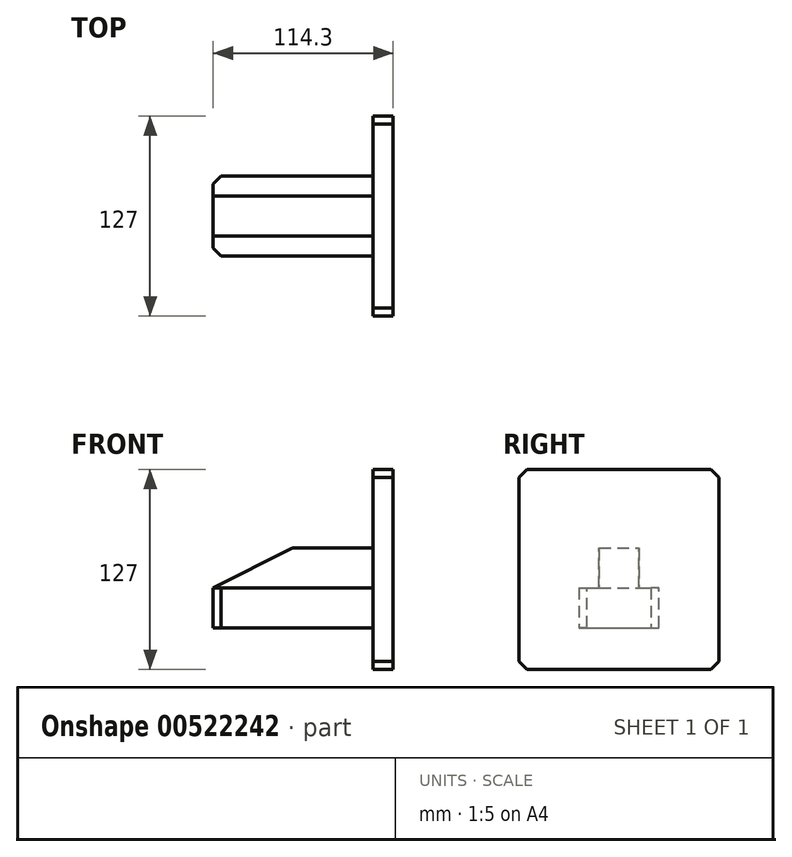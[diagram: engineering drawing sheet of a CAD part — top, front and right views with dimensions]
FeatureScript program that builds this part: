
annotation { "Feature Type Name" : "Feature", "Feature Type Description" : "" }
export const myFeature = defineFeature(function(context is Context, id is Id, definition is map)
    precondition{}
    {
        {
            var Q0;
            Q0=qCreatedBy(makeId("Front.planeOp"),FACE);
            var sketch = newSketch(context, id + "F0", { "sketchPlane" : qUnion([Q0])});
            skLineSegment(sketch, "E0.bottom", {"start": v(50.8, -12.7) * mm, "end": v(-50.8, -12.7) * mm});
            skLineSegment(sketch, "E0.top", {"start": v(50.8, 12.7) * mm, "end": v(-50.8, 12.7) * mm});
            skLineSegment(sketch, "E0.left", {"start": v(50.8, -12.7) * mm, "end": v(50.8, 12.7) * mm});
            skLineSegment(sketch, "E0.right", {"start": v(-50.8, -12.7) * mm, "end": v(-50.8, 12.7) * mm});
            skPoint(sketch, "E0.middle", {"position": v(0, 0) * mm});
            skLineSegment(sketch, "E1", {"start": v(50.8, 12.7) * mm, "end": v(50.8, 38.1) * mm});
            skLineSegment(sketch, "E2", {"start": v(50.8, 38.1) * mm, "end": v(0, 38.1) * mm});
            skLineSegment(sketch, "E3", {"start": v(0, 38.1) * mm, "end": v(-50.8, 12.7) * mm});
            skLineSegment(sketch, "E4.bottom", {"start": v(50.8, 87.78) * mm, "end": v(63.5, 87.78) * mm});
            skLineSegment(sketch, "E4.top", {"start": v(50.8, -39.22) * mm, "end": v(63.5, -39.22) * mm});
            skLineSegment(sketch, "E4.left", {"start": v(50.8, 87.78) * mm, "end": v(50.8, -39.22) * mm});
            skLineSegment(sketch, "E4.right", {"start": v(63.5, 87.78) * mm, "end": v(63.5, -39.22) * mm});
            skSolve(sketch);
        }
        {
            var Q0;
            {var subQ0=sQuery(id+"F0.wireOp",EDGE,"E0.bottom");Q0=makeQuery(id+"F0.imprint","IMPRINT",FACE,{"disambiguationData":[TD([[makeQuery(id+"F0.imprint","IMPRINT",EDGE,{"derivedFrom":subQ0}),-1.0]])]});}
            extrude(context, id + "F1", {"entities" : qUnion([Q0]), "endBound" : BoundingType.SYMMETRIC, "depth" : 50.8 * mm, "offsetDistance" : 25.4 * mm});
        }
        {
            var Q0;
            {var subQ0=sQuery(id+"F0.wireOp",EDGE,"E0.top");Q0=makeQuery(id+"F0.imprint","IMPRINT",FACE,{"disambiguationData":[TD([[makeQuery(id+"F0.imprint","IMPRINT",EDGE,{"derivedFrom":subQ0}),-1.0]])]});}
            extrude(context, id + "F2", {"entities" : qUnion([Q0]), "operationType" : NewBodyOperationType.ADD, "endBound" : BoundingType.SYMMETRIC, "depth" : 25.4 * mm, "offsetDistance" : 25.4 * mm});
        }
        {
            var Q0;
            {var subQ3=sQuery(id+"F0.wireOp",EDGE,"E4.bottom");Q0=makeQuery(id+"F0.imprint","IMPRINT",FACE,{"disambiguationData":[TD([[makeQuery(id+"F0.imprint","IMPRINT",EDGE,{"derivedFrom":subQ3}),-1.0]])]});}
            extrude(context, id + "F3", {"entities" : qUnion([Q0]), "operationType" : NewBodyOperationType.ADD, "endBound" : BoundingType.SYMMETRIC, "depth" : 127 * mm, "offsetDistance" : 25.4 * mm});
        }
        {
            var Q0;
            Q0=makeQuery(id+"F2.opExtrude","SWEPT_EDGE",EDGE,{"disambiguationData":[OSD([sQuery(id+"F0.wireOp",EDGE,"E2"),sQuery(id+"F0.wireOp",EDGE,"E3")])]});
            fillet(context, id + "F4", {"entities" : qUnion([Q0]), "radius" : 5.08 * mm, "tangentPropagation" : true, "allowEdgeOverflow" : false});
        }
        {
            var Q0;
            Q0=makeQuery(id+"F3.opExtrude","CAP_EDGE",EDGE,{"disambiguationData":[OSD([sQuery(id+"F0.wireOp",EDGE,"E4.bottom")])],"isStart":true});
            var Q1;
            Q1=makeQuery(id+"F3.opExtrude","CAP_EDGE",EDGE,{"disambiguationData":[OSD([sQuery(id+"F0.wireOp",EDGE,"E4.bottom")])],"isStart":false});
            var Q2;
            Q2=makeQuery(id+"F3.opExtrude","CAP_EDGE",EDGE,{"disambiguationData":[OSD([sQuery(id+"F0.wireOp",EDGE,"E4.top")])],"isStart":true});
            var Q3;
            Q3=makeQuery(id+"F3.opExtrude","CAP_EDGE",EDGE,{"disambiguationData":[OSD([sQuery(id+"F0.wireOp",EDGE,"E4.top")])],"isStart":false});
            var Q4;
            Q4=makeQuery(id+"F1.opExtrude","CAP_EDGE",EDGE,{"disambiguationData":[OSD([sQuery(id+"F0.wireOp",EDGE,"E0.right")])],"isStart":true});
            var Q5;
            Q5=makeQuery(id+"F1.opExtrude","CAP_EDGE",EDGE,{"disambiguationData":[OSD([sQuery(id+"F0.wireOp",EDGE,"E0.right")])],"isStart":false});
            chamfer(context, id + "F5", {"entities" : qUnion([Q0, Q1, Q2, Q3, Q4, Q5]), "width" : 5.08 * mm, "tangentPropagation" : true});
        }
    });
